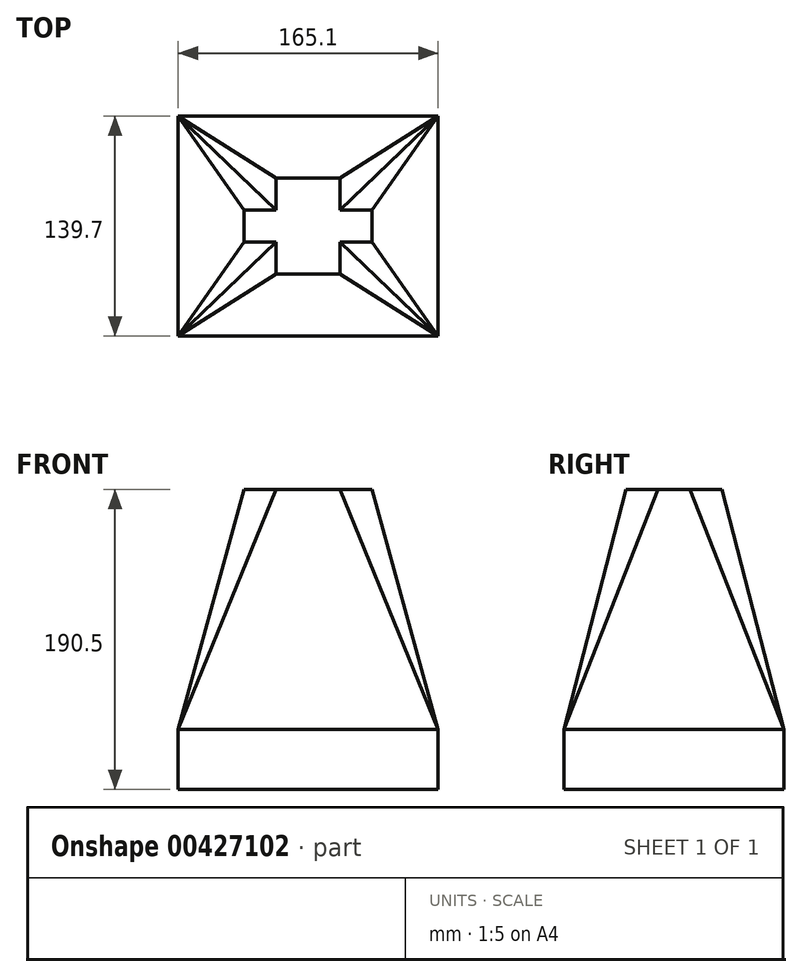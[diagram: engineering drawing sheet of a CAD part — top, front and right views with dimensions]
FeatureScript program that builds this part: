
annotation { "Feature Type Name" : "Feature", "Feature Type Description" : "" }
export const myFeature = defineFeature(function(context is Context, id is Id, definition is map)
    precondition{}
    {
        {
            var Q0;
            Q0=qCreatedBy(makeId("Top.planeOp"),FACE);
            var sketch = newSketch(context, id + "F0", { "sketchPlane" : qUnion([Q0])});
            skLineSegment(sketch, "E0.bottom", {"start": v(-82.55, -69.85) * mm, "end": v(82.55, -69.85) * mm});
            skLineSegment(sketch, "E0.top", {"start": v(-82.55, 69.85) * mm, "end": v(82.55, 69.85) * mm});
            skLineSegment(sketch, "E0.left", {"start": v(-82.55, -69.85) * mm, "end": v(-82.55, 69.85) * mm});
            skLineSegment(sketch, "E0.right", {"start": v(82.55, -69.85) * mm, "end": v(82.55, 69.85) * mm});
            skSolve(sketch);
        }
        {
            var Q0;
            Q0=makeQuery(id+"F0.imprint","IMPRINT",FACE,{"disambiguationData":[TD([[makeQuery(id+"F0.imprint","IMPRINT",EDGE,{"derivedFrom":sQuery(id+"F0.wireOp",EDGE,"E0.bottom")}),1.0]])]});
            extrude(context, id + "F1", {"entities" : qUnion([Q0]), "depth" : 38.1 * mm});
        }
        {
            var Q0;
            Q0=makeQuery(id+"F1.opExtrude","SWEPT_FACE",FACE,{"disambiguationData":[OSD([sQuery(id+"F0.wireOp",EDGE,"E0.bottom")])]});
            var sketch = newSketch(context, id + "F2", { "sketchPlane" : qUnion([Q0])});
            skLineSegment(sketch, "E1", {"start": v(-82.55, 38.1) * mm, "end": v(-20.32, 190.5) * mm});
            skLineSegment(sketch, "E2", {"start": v(-20.32, 190.5) * mm, "end": v(20.32, 190.5) * mm});
            skLineSegment(sketch, "E3", {"start": v(20.32, 190.5) * mm, "end": v(82.55, 38.1) * mm});
            skLineSegment(sketch, "E4", {"start": v(82.55, 38.1) * mm, "end": v(-82.55, 38.1) * mm});
            skSolve(sketch);
        }
        {
            var Q0;
            Q0=makeQuery(id+"F2.imprint","IMPRINT",FACE,{"disambiguationData":[TD([[makeQuery(id+"F2.imprint","IMPRINT",EDGE,{"derivedFrom":sQuery(id+"F2.wireOp",EDGE,"E1")}),-1.0]])]});
            extrude(context, id + "F3", {"entities" : qUnion([Q0]), "operationType" : NewBodyOperationType.ADD, "oppositeDirection" : true, "depth" : 139.7 * mm});
        }
        {
            var Q0;
            Q0=makeQuery(id+"F3.opExtrude","CAP_EDGE",EDGE,{"disambiguationData":[OSD([sQuery(id+"F2.wireOp",EDGE,"E2")])],"isStart":true});
            var Q1;
            Q1=makeQuery(id+"F3.opExtrude","CAP_EDGE",EDGE,{"disambiguationData":[OSD([sQuery(id+"F2.wireOp",EDGE,"E2")])],"isStart":false});
            chamfer(context, id + "F4", {"entities" : qUnion([Q0, Q1]), "chamferType" : ChamferType.TWO_OFFSETS, "width1" : 39.37 * mm, "oppositeDirection" : false, "width2" : 152.4 * mm, "tangentPropagation" : true});
        }
        {
            var Q0;
            Q0=makeQuery(id+"F1.opExtrude","SWEPT_FACE",FACE,{"disambiguationData":[OSD([sQuery(id+"F0.wireOp",EDGE,"E0.right")])]});
            var sketch = newSketch(context, id + "F5", { "sketchPlane" : qUnion([Q0])});
            skLineSegment(sketch, "E5", {"start": v(-69.85, 38.1) * mm, "end": v(69.85, 38.1) * mm});
            skLineSegment(sketch, "E6", {"start": v(69.85, 38.1) * mm, "end": v(10.16, 190.5) * mm});
            skLineSegment(sketch, "E7", {"start": v(10.16, 190.5) * mm, "end": v(-10.16, 190.5) * mm});
            skLineSegment(sketch, "E8", {"start": v(-10.16, 190.5) * mm, "end": v(-69.85, 38.1) * mm});
            skSolve(sketch);
        }
        {
            var Q0;
            Q0=makeQuery(id+"F5.imprint","IMPRINT",FACE,{"disambiguationData":[TD([[makeQuery(id+"F5.imprint","IMPRINT",EDGE,{"derivedFrom":sQuery(id+"F5.wireOp",EDGE,"E5")}),1.0]])]});
            extrude(context, id + "F6", {"entities" : qUnion([Q0]), "operationType" : NewBodyOperationType.ADD, "oppositeDirection" : true, "depth" : 165.1 * mm});
        }
        {
            var Q0;
            Q0=makeQuery(id+"F6.opExtrude","CAP_EDGE",EDGE,{"disambiguationData":[OSD([sQuery(id+"F5.wireOp",EDGE,"E7")])],"isStart":true});
            var Q1;
            Q1=makeQuery(id+"F6.opExtrude","CAP_EDGE",EDGE,{"disambiguationData":[OSD([sQuery(id+"F5.wireOp",EDGE,"E7")])],"isStart":false});
            chamfer(context, id + "F7", {"entities" : qUnion([Q0, Q1]), "chamferType" : ChamferType.TWO_OFFSETS, "width1" : 152.4 * mm, "oppositeDirection" : false, "width2" : 41.9 * mm, "tangentPropagation" : true});
        }
    });
